# Revit family: Hair-Dryer_World-Dryer_AirStyle-Recessed
name_source: partatom
category: Electrical Fixtures
revit_build: Autodesk Revit Architecture 2012 (Build: 20110309_2315(x64)
units: mm (PartAtom-declared; Revit-internal decimal feet)

## types (1)
- Hair-Dryer_World-Dryer_AirStyle-Recessed
    ADA Compliant = No
    Actuation = as Specified
    Air Output = as Specified
    Air Temperature = as Specified
    Assembly Code = C1030210
    Automatic = No
    Construction Details = http://www.arcat.com
    Cover Material = Metal - World Dryer - Cast Iron
    Default Elevation = 4' - 0"
    Description = World Dryer Electric Hand Dryer as Specified
    Drying Time = as Specified
    Expected Lifespan (Years) = 0
    Frequency = 0 Hz
    Green Building-LEED = http://www.arcat.com
    Hardware Finish = Metal - World Dryer - Brushed Chrome
    Installation-Fabrication = http://www.worlddryer.com
    Keynote = 10810
    MEP Amperage = 0 A
    MEP Apparent Power = 0 VA
    Maintenance Schedule (Months) = 0
    Manufacturer = World Dryer
    Manufacturer Fax = 708-449-6958
    Manufacturer Website = http://www.worlddryer.com
    Model = As Specified
    Product Data = http://www.arcat.com
    Product Properties = http://www.arcat.com
    Revision = R1_7_2012
    Sales Information = http://www.worlddryer.com
    Send Message = http://www.arcat.com
    Sound Pressure = 66 dB
    Specification = http://www.arcat.com
    Standards Conformance = as Specified
    Surface Finish = Metal - World Dryer - White
    URL = http://www.worlddryer.com
    Unit Depth = 0' - 6 3/32"
    Unit Length = 1' - 1 13/16"
    Unit Weight = 0
    Unit Width = 1' - 1 3/16"
    Voltage_MEP = 0 V
    Warranty Duration (Years) = 0

## geometry (parser evidence)
native form markers: Blend x4, Sweep x4
no freeform markers — native parametric forms only
